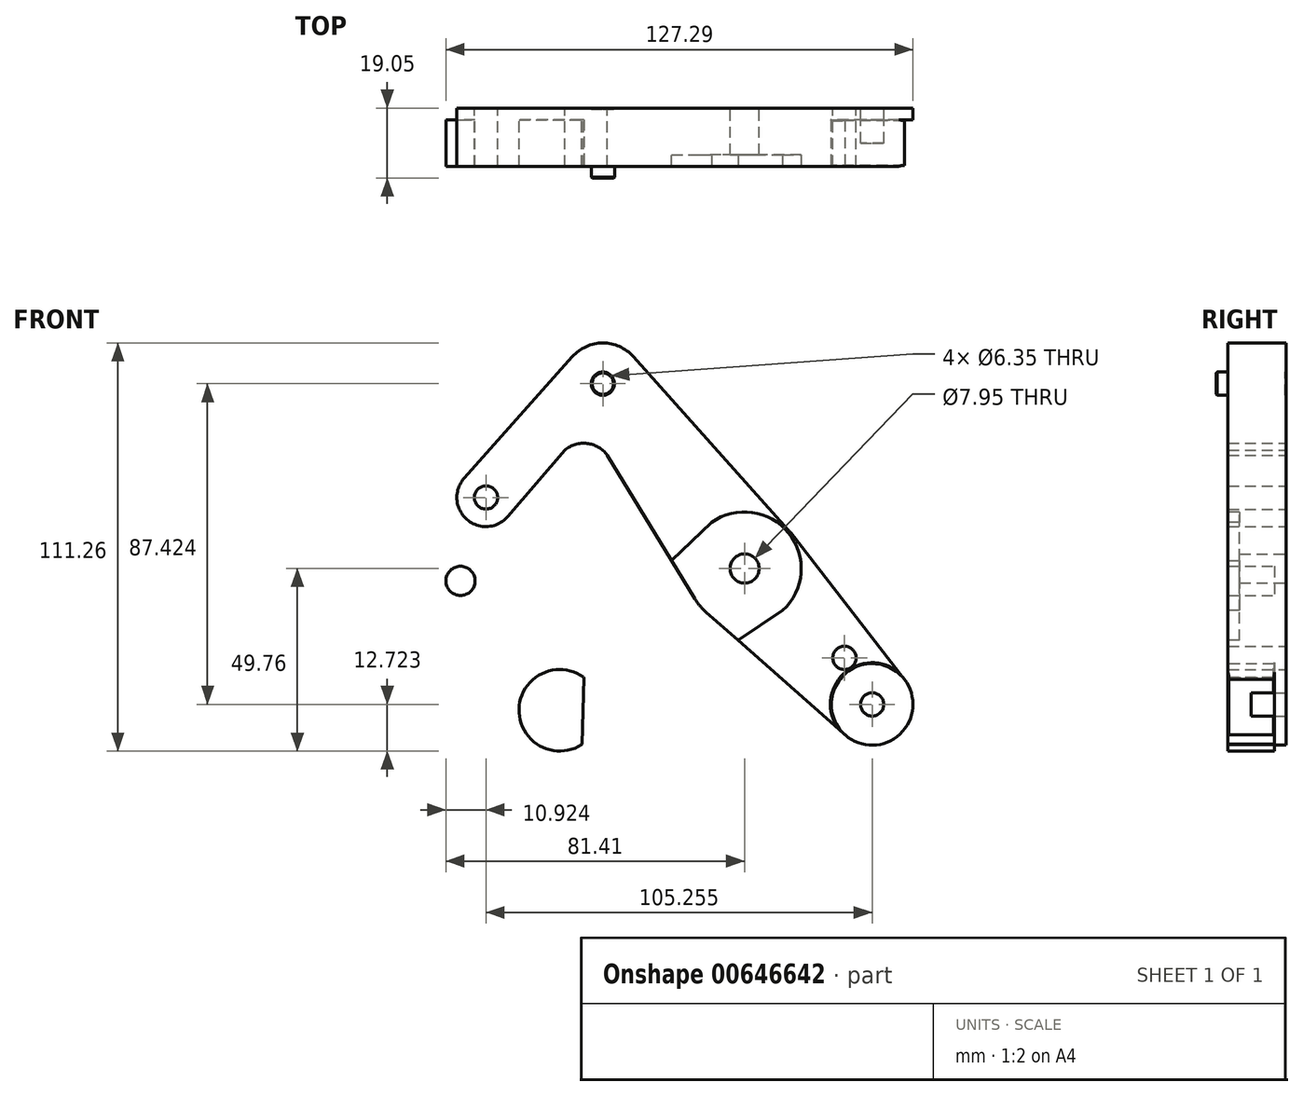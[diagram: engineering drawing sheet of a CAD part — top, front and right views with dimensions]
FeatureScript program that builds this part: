
annotation { "Feature Type Name" : "Feature", "Feature Type Description" : "" }
export const myFeature = defineFeature(function(context is Context, id is Id, definition is map)
    precondition{}
    {
        {
            var Q0;
            Q0=qCreatedBy(makeId("Front.planeOp"),FACE);
            var sketch = newSketch(context, id + "F0", { "sketchPlane" : qUnion([Q0])});
            skCircle(sketch, "E0", {"center": v(0, 0) * mm, "radius": 3.98 * mm});
            skCircle(sketch, "E1", {"center": v(0, 0) * mm, "radius": 15.88 * mm});
            skCircle(sketch, "E2", {"center": v(-38.65, 50.39) * mm, "radius": 11.11 * mm});
            skCircle(sketch, "E3", {"center": v(-38.65, 50.39) * mm, "radius": 3.18 * mm});
            skCircle(sketch, "E4", {"center": v(-70.49, 19.37) * mm, "radius": 3.18 * mm});
            skCircle(sketch, "E5", {"center": v(-70.49, 19.37) * mm, "radius": 7.94 * mm});
            skCircle(sketch, "E6", {"center": v(0, 0) * mm, "radius": 3.18 * mm});
            skCircle(sketch, "E7", {"center": v(34.77, -37.04) * mm, "radius": 3.18 * mm});
            skCircle(sketch, "E8", {"center": v(34.77, -37.04) * mm, "radius": 11.11 * mm});
            skLineSegment(sketch, "E9", {"start": v(-38.65, 50.39) * mm, "end": v(-70.49, 19.37) * mm, "construction": true});
            skLineSegment(sketch, "E10", {"start": v(-38.65, 50.39) * mm, "end": v(0, 0) * mm, "construction": true});
            skLineSegment(sketch, "E11", {"start": v(0, 0) * mm, "end": v(34.77, -37.04) * mm, "construction": true});
            skCircle(sketch, "E12", {"center": v(27.22, -24.36) * mm, "radius": 3.18 * mm});
            skLineSegment(sketch, "E13", {"start": v(0, 0) * mm, "end": v(-50.39, -38.65) * mm, "construction": true});
            skCircle(sketch, "E14", {"center": v(-50.39, -38.65) * mm, "radius": 11.11 * mm});
            skCircle(sketch, "E15", {"center": v(-50.39, -38.65) * mm, "radius": 3.18 * mm});
            skCircle(sketch, "E16", {"center": v(-34, -26.08) * mm, "radius": 3.18 * mm});
            skLineSegment(sketch, "E17", {"start": v(-50.39, -38.65) * mm, "end": v(-77.44, -3.38) * mm, "construction": true});
            skCircle(sketch, "E18", {"center": v(-77.44, -3.38) * mm, "radius": 3.18 * mm});
            skCircle(sketch, "E19", {"center": v(-77.44, -3.38) * mm, "radius": 7.94 * mm});
            skLineSegment(sketch, "E20", {"start": v(-30.36, 57.8) * mm, "end": v(11.84, 10.58) * mm});
            skLineSegment(sketch, "E21", {"start": v(12.54, 9.73) * mm, "end": v(43.55, -30.22) * mm});
            skLineSegment(sketch, "E22", {"start": v(-10.5, -11.9) * mm, "end": v(27.42, -45.37) * mm});
            skLineSegment(sketch, "E23", {"start": v(-46.95, 57.77) * mm, "end": v(-76.42, 24.65) * mm});
            skLineSegment(sketch, "E24", {"start": v(-84.07, -7.74) * mm, "end": v(-59.66, -44.76) * mm});
            skLineSegment(sketch, "E25", {"start": v(8.69, -13.29) * mm, "end": v(-44.3, -47.95) * mm});
            skArc(sketch, "E26", {"start": v(-49, 32.25) * mm, "mid": v(-42.92, 34.1) * mm, "end": v(-37.42, 30.91) * mm});
            skLineSegment(sketch, "E27", {"start": v(-13.56, -8.26) * mm, "end": v(-37.42, 30.91) * mm});
            skLineSegment(sketch, "E28", {"start": v(-49, 32.25) * mm, "end": v(-64.46, 14.2) * mm});
            skArc(sketch, "E29", {"start": v(-41.92, -18.6) * mm, "mid": v(-48.48, -22.05) * mm, "end": v(-55.03, -18.6) * mm});
            skLineSegment(sketch, "E30", {"start": v(-11.07, 11.38) * mm, "end": v(-41.92, -18.6) * mm});
            skLineSegment(sketch, "E31", {"start": v(-55.03, -18.6) * mm, "end": v(-71.25, 1.6) * mm});
            skLineSegment(sketch, "E32", {"start": v(-70.49, 19.37) * mm, "end": v(-77.44, -3.38) * mm, "construction": true});
            skSolve(sketch);
        }
        {
            var Q0;
            Q0=makeQuery(id+"F0.imprint","IMPRINT",FACE,{"disambiguationData":[TD([[makeQuery(id+"F0.imprint","IMPRINT",EDGE,{"derivedFrom":sQuery(id+"F0.wireOp",EDGE,"E0")}),-1.0]])]});
            var Q1;
            Q1=makeQuery(id+"F0.imprint","IMPRINT",FACE,{"disambiguationData":[TD([[makeQuery(id+"F0.imprint","IMPRINT",EDGE,{"derivedFrom":sQuery(id+"F0.wireOp",EDGE,"E12")}),-1.0]])]});
            var Q2;
            Q2=makeQuery(id+"F0.imprint","IMPRINT",FACE,{"disambiguationData":[TD([[makeQuery(id+"F0.imprint","IMPRINT",EDGE,{"derivedFrom":sQuery(id+"F0.wireOp",EDGE,"E7")}),-1.0]])]});
            var Q3;
            {var subQ0=sQuery(id+"F0.wireOp",EDGE,"E20");Q3=makeQuery(id+"F0.imprint","IMPRINT",FACE,{"disambiguationData":[TD([[makeQuery(id+"F0.imprint","IMPRINT",EDGE,{"derivedFrom":subQ0}),-1.0]])]});}
            var Q4;
            Q4=makeQuery(id+"F0.imprint","IMPRINT",FACE,{"disambiguationData":[TD([[makeQuery(id+"F0.imprint","IMPRINT",EDGE,{"derivedFrom":sQuery(id+"F0.wireOp",EDGE,"E3")}),-1.0]])]});
            var Q5;
            Q5=makeQuery(id+"F0.imprint","IMPRINT",FACE,{"disambiguationData":[TD([[makeQuery(id+"F0.imprint","IMPRINT",EDGE,{"derivedFrom":sQuery(id+"F0.wireOp",EDGE,"E4")}),-1.0]])]});
            var Q6;
            {var subQ0=sQuery(id+"F0.wireOp",EDGE,"E22");var subQ1=sQuery(id+"F0.wireOp",EDGE,"E1");var subQ2=makeQuery(id+"F0.imprint","INTERSECT",VERTEX,{"derivedFrom":[subQ1,subQ0]});Q6=makeQuery(id+"F0.imprint","IMPRINT",FACE,{"disambiguationData":[TD([[makeQuery(id+"F0.imprint","IMPRINT",EDGE,{"disambiguationData":[TD([[subQ2,-1.0]])],"derivedFrom":subQ1}),-1.0]])]});}
            var Q7;
            {var subQ0=sQuery(id+"F0.wireOp",EDGE,"E27");var subQ1=sQuery(id+"F0.wireOp",EDGE,"E1");var subQ2=makeQuery(id+"F0.imprint","INTERSECT",VERTEX,{"derivedFrom":[subQ1,subQ0]});Q7=makeQuery(id+"F0.imprint","IMPRINT",FACE,{"disambiguationData":[TD([[makeQuery(id+"F0.imprint","IMPRINT",EDGE,{"disambiguationData":[TD([[subQ2,1.0]])],"derivedFrom":subQ1}),-1.0]])]});}
            extrude(context, id + "F1", {"entities" : qUnion([Q0, Q1, Q2, Q3, Q4, Q5, Q6, Q7]), "depth" : 3.17 * mm, "offsetDistance" : 25.4 * mm});
        }
        {
            var Q0;
            Q0=makeQuery(id+"F0.imprint","IMPRINT",FACE,{"disambiguationData":[TD([[makeQuery(id+"F0.imprint","IMPRINT",EDGE,{"derivedFrom":sQuery(id+"F0.wireOp",EDGE,"E16")}),-1.0]])]});
            var Q1;
            Q1=makeQuery(id+"F0.imprint","IMPRINT",FACE,{"disambiguationData":[TD([[makeQuery(id+"F0.imprint","IMPRINT",EDGE,{"derivedFrom":sQuery(id+"F0.wireOp",EDGE,"E0")}),-1.0]])]});
            var Q2;
            Q2=makeQuery(id+"F0.imprint","IMPRINT",FACE,{"disambiguationData":[TD([[makeQuery(id+"F0.imprint","IMPRINT",EDGE,{"derivedFrom":sQuery(id+"F0.wireOp",EDGE,"E15")}),-1.0]])]});
            var Q3;
            Q3=makeQuery(id+"F0.imprint","IMPRINT",FACE,{"disambiguationData":[TD([[makeQuery(id+"F0.imprint","IMPRINT",EDGE,{"derivedFrom":sQuery(id+"F0.wireOp",EDGE,"E18")}),-1.0]])]});
            extrude(context, id + "F2", {"entities" : qUnion([Q0, Q1, Q2, Q3]), "operationType" : NewBodyOperationType.ADD, "depth" : 3.17 * mm, "offsetDistance" : 25.4 * mm});
        }
        {
            var Q0;
            {var subQ0=sQuery(id+"F0.wireOp",EDGE,"E27");var subQ1=sQuery(id+"F0.wireOp",EDGE,"E22");var subQ2=sQuery(id+"F0.wireOp",EDGE,"E1");var subQ3=sQuery(id+"F0.wireOp",EDGE,"E0");Q0=makeQuery(id+"F2.boolean.opBoolean","MERGE",FACE,{"derivedFrom":[makeQuery(id+"F1.opExtrude","CAP_FACE",FACE,{"disambiguationData":[OSD([subQ3,subQ2,sQuery(id+"F0.wireOp",EDGE,"E2"),sQuery(id+"F0.wireOp",EDGE,"E3"),sQuery(id+"F0.wireOp",EDGE,"E4"),sQuery(id+"F0.wireOp",EDGE,"E5"),sQuery(id+"F0.wireOp",EDGE,"E7"),sQuery(id+"F0.wireOp",EDGE,"E8"),sQuery(id+"F0.wireOp",EDGE,"E12"),sQuery(id+"F0.wireOp",EDGE,"E20"),sQuery(id+"F0.wireOp",EDGE,"E21"),subQ1,sQuery(id+"F0.wireOp",EDGE,"E23"),sQuery(id+"F0.wireOp",EDGE,"E26"),subQ0,sQuery(id+"F0.wireOp",EDGE,"E28")])],"isStart":false}),makeQuery(id+"F2.opExtrude","CAP_FACE",FACE,{"disambiguationData":[OSD([subQ3,subQ2,sQuery(id+"F0.wireOp",EDGE,"E14"),sQuery(id+"F0.wireOp",EDGE,"E15"),sQuery(id+"F0.wireOp",EDGE,"E16"),sQuery(id+"F0.wireOp",EDGE,"E18"),sQuery(id+"F0.wireOp",EDGE,"E19"),subQ1,sQuery(id+"F0.wireOp",EDGE,"E24"),sQuery(id+"F0.wireOp",EDGE,"E25"),subQ0,sQuery(id+"F0.wireOp",EDGE,"E29"),sQuery(id+"F0.wireOp",EDGE,"E30"),sQuery(id+"F0.wireOp",EDGE,"E31")])],"isStart":false})]});}
            var sketch = newSketch(context, id + "F3", { "sketchPlane" : qUnion([Q0])});
            skCircle(sketch, "E33", {"center": v(0, 0) * mm, "radius": 15.44 * mm});
            skCircle(sketch, "E34", {"center": v(-50.39, -38.65) * mm, "radius": 10.88 * mm});
            skCircle(sketch, "E35", {"center": v(-77.44, -3.38) * mm, "radius": 7.94 * mm});
            skLineSegment(sketch, "E36", {"start": v(-71.25, 1.6) * mm, "end": v(-55.03, -18.6) * mm});
            skLineSegment(sketch, "E37", {"start": v(-41.92, -18.6) * mm, "end": v(-9, 12.54) * mm});
            skLineSegment(sketch, "E38", {"start": v(-44.3, -47.95) * mm, "end": v(10.37, -11.44) * mm});
            skLineSegment(sketch, "E39", {"start": v(-84.07, -7.74) * mm, "end": v(-59.66, -44.76) * mm});
            skArc(sketch, "E40", {"start": v(-55.03, -18.6) * mm, "mid": v(-48.48, -21.74) * mm, "end": v(-41.92, -18.6) * mm});
            skSolve(sketch);
        }
        {
            var Q0;
            Q0=makeQuery(id+"F3.imprint","IMPRINT",FACE,{"disambiguationData":[TD([[makeQuery(id+"F3.imprint","IMPRINT",EDGE,{"derivedFrom":makeQuery(id+"F2.opExtrude","CAP_EDGE",EDGE,{"disambiguationData":[OSD([sQuery(id+"F0.wireOp",EDGE,"E18")])],"isStart":false})}),-1.0]])]});
            var Q1;
            Q1=makeQuery(id+"F3.imprint","IMPRINT",FACE,{"disambiguationData":[TD([[makeQuery(id+"F3.imprint","IMPRINT",EDGE,{"derivedFrom":sQuery(id+"F3.wireOp",EDGE,"E34")}),-1.0]])]});
            var Q2;
            Q2=makeQuery(id+"F3.imprint","IMPRINT",FACE,{"disambiguationData":[TD([[makeQuery(id+"F3.imprint","IMPRINT",EDGE,{"derivedFrom":makeQuery(id+"F1.opExtrude","CAP_EDGE",EDGE,{"disambiguationData":[OSD([sQuery(id+"F0.wireOp",EDGE,"E0")])],"isStart":false})}),-1.0]])]});
            var Q3;
            Q3=makeQuery(id+"F3.imprint","IMPRINT",FACE,{"disambiguationData":[TD([[makeQuery(id+"F3.imprint","IMPRINT",EDGE,{"derivedFrom":sQuery(id+"F3.wireOp",EDGE,"E34")}),1.0]])]});
            extrude(context, id + "F4", {"entities" : qUnion([Q0, Q1, Q2, Q3]), "depth" : 3.17 * mm, "offsetDistance" : 25.4 * mm});
        }
        {
            var Q0;
            Q0=makeQuery(id+"F0.imprint","IMPRINT",FACE,{"disambiguationData":[TD([[makeQuery(id+"F0.imprint","IMPRINT",EDGE,{"derivedFrom":sQuery(id+"F0.wireOp",EDGE,"E16")}),-1.0]])]});
            var Q1;
            Q1=makeQuery(id+"F0.imprint","IMPRINT",FACE,{"disambiguationData":[TD([[makeQuery(id+"F0.imprint","IMPRINT",EDGE,{"derivedFrom":sQuery(id+"F0.wireOp",EDGE,"E15")}),-1.0]])]});
            var Q2;
            Q2=makeQuery(id+"F0.imprint","IMPRINT",FACE,{"disambiguationData":[TD([[makeQuery(id+"F0.imprint","IMPRINT",EDGE,{"derivedFrom":sQuery(id+"F0.wireOp",EDGE,"E18")}),-1.0]])]});
            extrude(context, id + "F5", {"entities" : qUnion([Q0, Q1, Q2]), "operationType" : NewBodyOperationType.REMOVE, "depth" : 62.74 * mm, "offsetDistance" : 25.4 * mm});
        }
        {
            var Q0;
            Q0=qCreatedBy(makeId("Front.planeOp"),FACE);
            cPlane(context, id + "F6", {"entities" : qUnion([Q0]), "cplaneType" : CPlaneType.OFFSET, "offset" : 9.52 * mm, "width" : 152.4 * mm, "height" : 152.4 * mm});
        }
        {
            var Q0;
            Q0=makeQuery(id+"F4.opExtrude","CAP_FACE",FACE,{"disambiguationData":[OSD([sQuery(id+"F0.wireOp",EDGE,"E0"),sQuery(id+"F0.wireOp",EDGE,"E14"),sQuery(id+"F0.wireOp",EDGE,"E15"),sQuery(id+"F0.wireOp",EDGE,"E16"),sQuery(id+"F0.wireOp",EDGE,"E18"),sQuery(id+"F0.wireOp",EDGE,"E29"),sQuery(id+"F3.wireOp",EDGE,"E33"),sQuery(id+"F3.wireOp",EDGE,"E35"),sQuery(id+"F3.wireOp",EDGE,"E36"),sQuery(id+"F3.wireOp",EDGE,"E37"),sQuery(id+"F3.wireOp",EDGE,"E38"),sQuery(id+"F3.wireOp",EDGE,"E39")])],"isStart":true});
            var sketch = newSketch(context, id + "F7", { "sketchPlane" : qUnion([Q0])});
            skCircle(sketch, "E41", {"center": v(77.44, -3.38) * mm, "radius": 3.98 * mm});
            skArc(sketch, "E42", {"start": v(44.3, -47.95) * mm, "mid": v(61.5, -38.32) * mm, "end": v(43.77, -29.71) * mm});
            skLineSegment(sketch, "E43", {"start": v(43.77, -29.71) * mm, "end": v(44.3, -47.95) * mm});
            skSolve(sketch);
        }
        {
            var Q0;
            {var subQ0=sQuery(id+"F0.wireOp",EDGE,"E27");var subQ1=sQuery(id+"F0.wireOp",EDGE,"E22");var subQ2=sQuery(id+"F0.wireOp",EDGE,"E1");var subQ3=sQuery(id+"F0.wireOp",EDGE,"E0");Q0=makeQuery(id+"F2.boolean.opBoolean","MERGE",FACE,{"derivedFrom":[makeQuery(id+"F1.opExtrude","CAP_FACE",FACE,{"disambiguationData":[OSD([subQ3,subQ2,sQuery(id+"F0.wireOp",EDGE,"E2"),sQuery(id+"F0.wireOp",EDGE,"E3"),sQuery(id+"F0.wireOp",EDGE,"E4"),sQuery(id+"F0.wireOp",EDGE,"E5"),sQuery(id+"F0.wireOp",EDGE,"E7"),sQuery(id+"F0.wireOp",EDGE,"E8"),sQuery(id+"F0.wireOp",EDGE,"E12"),sQuery(id+"F0.wireOp",EDGE,"E20"),sQuery(id+"F0.wireOp",EDGE,"E21"),subQ1,sQuery(id+"F0.wireOp",EDGE,"E23"),sQuery(id+"F0.wireOp",EDGE,"E26"),subQ0,sQuery(id+"F0.wireOp",EDGE,"E28")])],"isStart":true}),makeQuery(id+"F2.opExtrude","CAP_FACE",FACE,{"disambiguationData":[OSD([subQ3,subQ2,sQuery(id+"F0.wireOp",EDGE,"E14"),sQuery(id+"F0.wireOp",EDGE,"E15"),sQuery(id+"F0.wireOp",EDGE,"E16"),sQuery(id+"F0.wireOp",EDGE,"E18"),sQuery(id+"F0.wireOp",EDGE,"E19"),subQ1,sQuery(id+"F0.wireOp",EDGE,"E24"),sQuery(id+"F0.wireOp",EDGE,"E25"),subQ0,sQuery(id+"F0.wireOp",EDGE,"E29"),sQuery(id+"F0.wireOp",EDGE,"E30"),sQuery(id+"F0.wireOp",EDGE,"E31")])],"isStart":true})]});}
            var sketch = newSketch(context, id + "F8", { "sketchPlane" : qUnion([Q0])});
            skCircle(sketch, "E44", {"center": v(-34.77, -37.04) * mm, "radius": 11.11 * mm});
            skCircle(sketch, "E45", {"center": v(0, 0) * mm, "radius": 3.98 * mm});
            skCircle(sketch, "E46", {"center": v(38.65, 50.39) * mm, "radius": 3.98 * mm});
            skSolve(sketch);
        }
        {
            var Q0;
            Q0=makeQuery(id+"F7.imprint","IMPRINT",FACE,{"disambiguationData":[TD([[makeQuery(id+"F7.imprint","IMPRINT",EDGE,{"derivedFrom":sQuery(id+"F7.wireOp",EDGE,"E41")}),1.0]])]});
            var Q1;
            Q1=makeQuery(id+"F7.imprint","IMPRINT",FACE,{"disambiguationData":[TD([[makeQuery(id+"F7.imprint","IMPRINT",EDGE,{"derivedFrom":makeQuery(id+"F4.opExtrude","CAP_EDGE",EDGE,{"disambiguationData":[OSD([sQuery(id+"F0.wireOp",EDGE,"E18")])],"isStart":true})}),-1.0]])]});
            var Q2;
            {var subQ0=sQuery(id+"F8.wireOp",EDGE,"E44");Q2=makeQuery(id+"F8.imprint","IMPRINT",FACE,{"disambiguationData":[TD([[makeQuery(id+"F8.imprint","IMPRINT",EDGE,{"disambiguationData":[OD(0.0)],"derivedFrom":subQ0}),-1.0]])]});}
            var Q3;
            Q3=makeQuery(id+"F8.imprint","IMPRINT",FACE,{"disambiguationData":[TD([[makeQuery(id+"F8.imprint","IMPRINT",EDGE,{"derivedFrom":makeQuery(id+"F1.opExtrude","CAP_EDGE",EDGE,{"disambiguationData":[OSD([sQuery(id+"F0.wireOp",EDGE,"E7")])],"isStart":true})}),-1.0]])]});
            var Q4;
            Q4=makeQuery(id+"F8.imprint","IMPRINT",FACE,{"disambiguationData":[TD([[makeQuery(id+"F8.imprint","IMPRINT",EDGE,{"derivedFrom":sQuery(id+"F8.wireOp",EDGE,"E46")}),1.0]])]});
            var Q5;
            Q5=makeQuery(id+"F8.imprint","IMPRINT",FACE,{"disambiguationData":[TD([[makeQuery(id+"F8.imprint","IMPRINT",EDGE,{"derivedFrom":makeQuery(id+"F1.opExtrude","CAP_EDGE",EDGE,{"disambiguationData":[OSD([sQuery(id+"F0.wireOp",EDGE,"E3")])],"isStart":true})}),-1.0]])]});
            var Q6;
            {var subQ2=sQuery(id+"F7.wireOp",EDGE,"E43");Q6=makeQuery(id+"F7.imprint","IMPRINT",FACE,{"disambiguationData":[TD([[makeQuery(id+"F7.imprint","IMPRINT",EDGE,{"derivedFrom":subQ2}),1.0]])]});}
            var Q7;
            Q7=makeQuery(id+"F7.imprint","IMPRINT",FACE,{"disambiguationData":[TD([[makeQuery(id+"F7.imprint","IMPRINT",EDGE,{"derivedFrom":makeQuery(id+"F4.opExtrude","CAP_EDGE",EDGE,{"disambiguationData":[OSD([sQuery(id+"F0.wireOp",EDGE,"E15")])],"isStart":true})}),-1.0]])]});
            var Q8;
            Q8=qCreatedBy(id+"F6.planeOp",FACE);
            extrude(context, id + "F9", {"entities" : qUnion([Q0, Q1, Q2, Q3, Q4, Q5, Q6, Q7]), "endBound" : BoundingType.UP_TO_SURFACE, "oppositeDirection" : true, "depth" : 25.4 * mm, "endBoundEntityFace" : qUnion([Q8]), "offsetDistance" : 25.4 * mm});
        }
        {
            var Q0;
            Q0=makeQuery(id+"F1.opExtrude","SWEPT_BODY",BODY,{"disambiguationData":[OSD([sQuery(id+"F0.wireOp",EDGE,"E0"),sQuery(id+"F0.wireOp",EDGE,"E1"),sQuery(id+"F0.wireOp",EDGE,"E2"),sQuery(id+"F0.wireOp",EDGE,"E3"),sQuery(id+"F0.wireOp",EDGE,"E4"),sQuery(id+"F0.wireOp",EDGE,"E5"),sQuery(id+"F0.wireOp",EDGE,"E7"),sQuery(id+"F0.wireOp",EDGE,"E8"),sQuery(id+"F0.wireOp",EDGE,"E12"),sQuery(id+"F0.wireOp",EDGE,"E20"),sQuery(id+"F0.wireOp",EDGE,"E21"),sQuery(id+"F0.wireOp",EDGE,"E22"),sQuery(id+"F0.wireOp",EDGE,"E23"),sQuery(id+"F0.wireOp",EDGE,"E26"),sQuery(id+"F0.wireOp",EDGE,"E27"),sQuery(id+"F0.wireOp",EDGE,"E28")])]});
            var Q1;
            Q1=makeQuery(id+"F4.opExtrude","SWEPT_BODY",BODY,{"disambiguationData":[OSD([sQuery(id+"F0.wireOp",EDGE,"E0"),sQuery(id+"F0.wireOp",EDGE,"E14"),sQuery(id+"F0.wireOp",EDGE,"E15"),sQuery(id+"F0.wireOp",EDGE,"E16"),sQuery(id+"F0.wireOp",EDGE,"E18"),sQuery(id+"F0.wireOp",EDGE,"E29"),sQuery(id+"F3.wireOp",EDGE,"E33"),sQuery(id+"F3.wireOp",EDGE,"E35"),sQuery(id+"F3.wireOp",EDGE,"E36"),sQuery(id+"F3.wireOp",EDGE,"E37"),sQuery(id+"F3.wireOp",EDGE,"E38"),sQuery(id+"F3.wireOp",EDGE,"E39")])]});
            var Q2;
            Q2=makeQuery(id+"F9.opExtrude","SWEPT_BODY",BODY,{"disambiguationData":[OSD([sQuery(id+"F7.wireOp",EDGE,"E41")])]});
            var Q3;
            Q3=makeQuery(id+"F9.opExtrude","SWEPT_BODY",BODY,{"disambiguationData":[OSD([sQuery(id+"F7.wireOp",EDGE,"E42"),sQuery(id+"F7.wireOp",EDGE,"E43")])]});
            var Q4;
            Q4=makeQuery(id+"F9.opExtrude","SWEPT_BODY",BODY,{"disambiguationData":[OSD([sQuery(id+"F8.wireOp",EDGE,"E44")])]});
            var Q5;
            Q5=makeQuery(id+"F9.opExtrude","SWEPT_BODY",BODY,{"disambiguationData":[OSD([sQuery(id+"F8.wireOp",EDGE,"E46")])]});
            booleanBodies(context, id + "F10", {"operationType" : BooleanOperationType.SUBTRACTION, "tools" : qUnion([Q0, Q1]), "targets" : qUnion([Q2, Q3, Q4, Q5]), "keepTools" : true});
        }
        {
            var Q0;
            {var subQ0=sQuery(id+"F0.wireOp",EDGE,"E27");var subQ1=sQuery(id+"F0.wireOp",EDGE,"E22");var subQ2=sQuery(id+"F0.wireOp",EDGE,"E1");var subQ3=sQuery(id+"F0.wireOp",EDGE,"E0");Q0=makeQuery(id+"F10.opBoolean","INTERSECT",EDGE,{"derivedFrom":[makeQuery(id+"F2.boolean.opBoolean","MERGE",FACE,{"derivedFrom":[makeQuery(id+"F1.opExtrude","CAP_FACE",FACE,{"disambiguationData":[OSD([subQ3,subQ2,sQuery(id+"F0.wireOp",EDGE,"E2"),sQuery(id+"F0.wireOp",EDGE,"E3"),sQuery(id+"F0.wireOp",EDGE,"E4"),sQuery(id+"F0.wireOp",EDGE,"E5"),sQuery(id+"F0.wireOp",EDGE,"E7"),sQuery(id+"F0.wireOp",EDGE,"E8"),sQuery(id+"F0.wireOp",EDGE,"E12"),sQuery(id+"F0.wireOp",EDGE,"E20"),sQuery(id+"F0.wireOp",EDGE,"E21"),subQ1,sQuery(id+"F0.wireOp",EDGE,"E23"),sQuery(id+"F0.wireOp",EDGE,"E26"),subQ0,sQuery(id+"F0.wireOp",EDGE,"E28")])],"isStart":false}),makeQuery(id+"F2.opExtrude","CAP_FACE",FACE,{"disambiguationData":[OSD([subQ3,subQ2,sQuery(id+"F0.wireOp",EDGE,"E14"),sQuery(id+"F0.wireOp",EDGE,"E15"),sQuery(id+"F0.wireOp",EDGE,"E16"),sQuery(id+"F0.wireOp",EDGE,"E18"),sQuery(id+"F0.wireOp",EDGE,"E19"),subQ1,sQuery(id+"F0.wireOp",EDGE,"E24"),sQuery(id+"F0.wireOp",EDGE,"E25"),subQ0,sQuery(id+"F0.wireOp",EDGE,"E29"),sQuery(id+"F0.wireOp",EDGE,"E30"),sQuery(id+"F0.wireOp",EDGE,"E31")])],"isStart":false})]}),makeQuery(id+"F9.opExtrude","SWEPT_FACE",FACE,{"disambiguationData":[OSD([sQuery(id+"F8.wireOp",EDGE,"E44")])]})]});}
            var Q1;
            Q1=makeQuery(id+"F9.opExtrude","CAP_FACE",FACE,{"disambiguationData":[OSD([sQuery(id+"F8.wireOp",EDGE,"E44")])],"isStart":true});
            var Q2;
            Q2=makeQuery(id+"F10.opBoolean","COPY",EDGE,{"derivedFrom":makeQuery(id+"F4.opExtrude","CAP_EDGE",EDGE,{"disambiguationData":[OSD([sQuery(id+"F0.wireOp",EDGE,"E15")])],"isStart":true})});
            var Q3;
            Q3=makeQuery(id+"F10.opBoolean","INTERSECT",EDGE,{"derivedFrom":[makeQuery(id+"F4.opExtrude","CAP_FACE",FACE,{"disambiguationData":[OSD([sQuery(id+"F0.wireOp",EDGE,"E0"),sQuery(id+"F0.wireOp",EDGE,"E14"),sQuery(id+"F0.wireOp",EDGE,"E15"),sQuery(id+"F0.wireOp",EDGE,"E16"),sQuery(id+"F0.wireOp",EDGE,"E18"),sQuery(id+"F0.wireOp",EDGE,"E29"),sQuery(id+"F3.wireOp",EDGE,"E33"),sQuery(id+"F3.wireOp",EDGE,"E35"),sQuery(id+"F3.wireOp",EDGE,"E36"),sQuery(id+"F3.wireOp",EDGE,"E37"),sQuery(id+"F3.wireOp",EDGE,"E38"),sQuery(id+"F3.wireOp",EDGE,"E39")])],"isStart":false}),makeQuery(id+"F9.opExtrude","SWEPT_FACE",FACE,{"disambiguationData":[OSD([sQuery(id+"F7.wireOp",EDGE,"E42")])]})]});
            var Q4;
            Q4=makeQuery(id+"F10.opBoolean","INTERSECT",EDGE,{"derivedFrom":[makeQuery(id+"F4.opExtrude","CAP_FACE",FACE,{"disambiguationData":[OSD([sQuery(id+"F0.wireOp",EDGE,"E0"),sQuery(id+"F0.wireOp",EDGE,"E14"),sQuery(id+"F0.wireOp",EDGE,"E15"),sQuery(id+"F0.wireOp",EDGE,"E16"),sQuery(id+"F0.wireOp",EDGE,"E18"),sQuery(id+"F0.wireOp",EDGE,"E29"),sQuery(id+"F3.wireOp",EDGE,"E33"),sQuery(id+"F3.wireOp",EDGE,"E35"),sQuery(id+"F3.wireOp",EDGE,"E36"),sQuery(id+"F3.wireOp",EDGE,"E37"),sQuery(id+"F3.wireOp",EDGE,"E38"),sQuery(id+"F3.wireOp",EDGE,"E39")])],"isStart":false}),makeQuery(id+"F9.opExtrude","SWEPT_FACE",FACE,{"disambiguationData":[OSD([sQuery(id+"F7.wireOp",EDGE,"E43")])]})]});
            var Q5;
            Q5=makeQuery(id+"F9.opExtrude","SWEPT_EDGE",EDGE,{"disambiguationData":[OSD([sQuery(id+"F3.wireOp",EDGE,"E38"),sQuery(id+"F7.wireOp",EDGE,"E42"),sQuery(id+"F7.wireOp",EDGE,"E43")])]});
            var Q6;
            Q6=makeQuery(id+"F9.opExtrude","SWEPT_EDGE",EDGE,{"disambiguationData":[OSD([sQuery(id+"F7.wireOp",EDGE,"E42"),sQuery(id+"F7.wireOp",EDGE,"E43")])]});
            var Q7;
            Q7=makeQuery(id+"F10.opBoolean","COPY",EDGE,{"derivedFrom":makeQuery(id+"F1.opExtrude","CAP_EDGE",EDGE,{"disambiguationData":[OSD([sQuery(id+"F0.wireOp",EDGE,"E3")])],"isStart":true})});
            var Q8;
            {var subQ0=sQuery(id+"F0.wireOp",EDGE,"E27");var subQ1=sQuery(id+"F0.wireOp",EDGE,"E22");var subQ2=sQuery(id+"F0.wireOp",EDGE,"E1");var subQ3=sQuery(id+"F0.wireOp",EDGE,"E0");Q8=makeQuery(id+"F10.opBoolean","INTERSECT",EDGE,{"derivedFrom":[makeQuery(id+"F2.boolean.opBoolean","MERGE",FACE,{"derivedFrom":[makeQuery(id+"F1.opExtrude","CAP_FACE",FACE,{"disambiguationData":[OSD([subQ3,subQ2,sQuery(id+"F0.wireOp",EDGE,"E2"),sQuery(id+"F0.wireOp",EDGE,"E3"),sQuery(id+"F0.wireOp",EDGE,"E4"),sQuery(id+"F0.wireOp",EDGE,"E5"),sQuery(id+"F0.wireOp",EDGE,"E7"),sQuery(id+"F0.wireOp",EDGE,"E8"),sQuery(id+"F0.wireOp",EDGE,"E12"),sQuery(id+"F0.wireOp",EDGE,"E20"),sQuery(id+"F0.wireOp",EDGE,"E21"),subQ1,sQuery(id+"F0.wireOp",EDGE,"E23"),sQuery(id+"F0.wireOp",EDGE,"E26"),subQ0,sQuery(id+"F0.wireOp",EDGE,"E28")])],"isStart":false}),makeQuery(id+"F2.opExtrude","CAP_FACE",FACE,{"disambiguationData":[OSD([subQ3,subQ2,sQuery(id+"F0.wireOp",EDGE,"E14"),sQuery(id+"F0.wireOp",EDGE,"E15"),sQuery(id+"F0.wireOp",EDGE,"E16"),sQuery(id+"F0.wireOp",EDGE,"E18"),sQuery(id+"F0.wireOp",EDGE,"E19"),subQ1,sQuery(id+"F0.wireOp",EDGE,"E24"),sQuery(id+"F0.wireOp",EDGE,"E25"),subQ0,sQuery(id+"F0.wireOp",EDGE,"E29"),sQuery(id+"F0.wireOp",EDGE,"E30"),sQuery(id+"F0.wireOp",EDGE,"E31")])],"isStart":false})]}),makeQuery(id+"F9.opExtrude","SWEPT_FACE",FACE,{"disambiguationData":[OSD([sQuery(id+"F8.wireOp",EDGE,"E46")])]})]});}
            var Q9;
            Q9=makeQuery(id+"F10.opBoolean","COPY",EDGE,{"derivedFrom":makeQuery(id+"F4.opExtrude","CAP_EDGE",EDGE,{"disambiguationData":[OSD([sQuery(id+"F0.wireOp",EDGE,"E18")])],"isStart":true})});
            var Q10;
            Q10=makeQuery(id+"F10.opBoolean","INTERSECT",EDGE,{"derivedFrom":[makeQuery(id+"F4.opExtrude","CAP_FACE",FACE,{"disambiguationData":[OSD([sQuery(id+"F0.wireOp",EDGE,"E0"),sQuery(id+"F0.wireOp",EDGE,"E14"),sQuery(id+"F0.wireOp",EDGE,"E15"),sQuery(id+"F0.wireOp",EDGE,"E16"),sQuery(id+"F0.wireOp",EDGE,"E18"),sQuery(id+"F0.wireOp",EDGE,"E29"),sQuery(id+"F3.wireOp",EDGE,"E33"),sQuery(id+"F3.wireOp",EDGE,"E35"),sQuery(id+"F3.wireOp",EDGE,"E36"),sQuery(id+"F3.wireOp",EDGE,"E37"),sQuery(id+"F3.wireOp",EDGE,"E38"),sQuery(id+"F3.wireOp",EDGE,"E39")])],"isStart":false}),makeQuery(id+"F9.opExtrude","SWEPT_FACE",FACE,{"disambiguationData":[OSD([sQuery(id+"F7.wireOp",EDGE,"E41")])]})]});
            chamfer(context, id + "F11", {"entities" : qUnion([Q0, Q1, Q2, Q3, Q4, Q5, Q6, Q7, Q8, Q9, Q10]), "width" : 0.25 * mm, "tangentPropagation" : true});
        }
        {
            var Q0;
            Q0=makeQuery(id+"F9.opExtrude","SWEPT_BODY",BODY,{"disambiguationData":[OSD([sQuery(id+"F8.wireOp",EDGE,"E44")])]});
            var Q1;
            Q1=makeQuery(id+"F9.opExtrude","SWEPT_BODY",BODY,{"disambiguationData":[OSD([sQuery(id+"F7.wireOp",EDGE,"E42"),sQuery(id+"F7.wireOp",EDGE,"E43")])]});
            var Q2;
            Q2=makeQuery(id+"F9.opExtrude","SWEPT_BODY",BODY,{"disambiguationData":[OSD([sQuery(id+"F7.wireOp",EDGE,"E41")])]});
            var Q3;
            Q3=makeQuery(id+"F9.opExtrude","SWEPT_BODY",BODY,{"disambiguationData":[OSD([sQuery(id+"F8.wireOp",EDGE,"E46")])]});
            var Q4;
            Q4=qCreatedBy(id+"F6.planeOp",FACE);
            mirror(context, id + "F12", {"operationType" : NewBodyOperationType.ADD, "entities" : qUnion([Q0, Q1, Q2, Q3]), "mirrorPlane" : qUnion([Q4])});
        }
        {
            var Q0;
            Q0=makeQuery(id+"F9.opExtrude","SWEPT_BODY",BODY,{"disambiguationData":[OSD([sQuery(id+"F7.wireOp",EDGE,"E42"),sQuery(id+"F7.wireOp",EDGE,"E43")])]});
            var Q1;
            Q1=makeQuery(id+"F9.opExtrude","SWEPT_BODY",BODY,{"disambiguationData":[OSD([sQuery(id+"F7.wireOp",EDGE,"E41")])]});
            var Q2;
            Q2=makeQuery(id+"F9.opExtrude","SWEPT_BODY",BODY,{"disambiguationData":[OSD([sQuery(id+"F8.wireOp",EDGE,"E44")])]});
            var Q3;
            Q3=makeQuery(id+"F9.opExtrude","SWEPT_BODY",BODY,{"disambiguationData":[OSD([sQuery(id+"F8.wireOp",EDGE,"E46")])]});
            booleanBodies(context, id + "F13", {"operationType" : BooleanOperationType.INTERSECTION, "tools" : qUnion([Q0, Q1, Q2, Q3]), "keepTools" : true});
        }
    });
